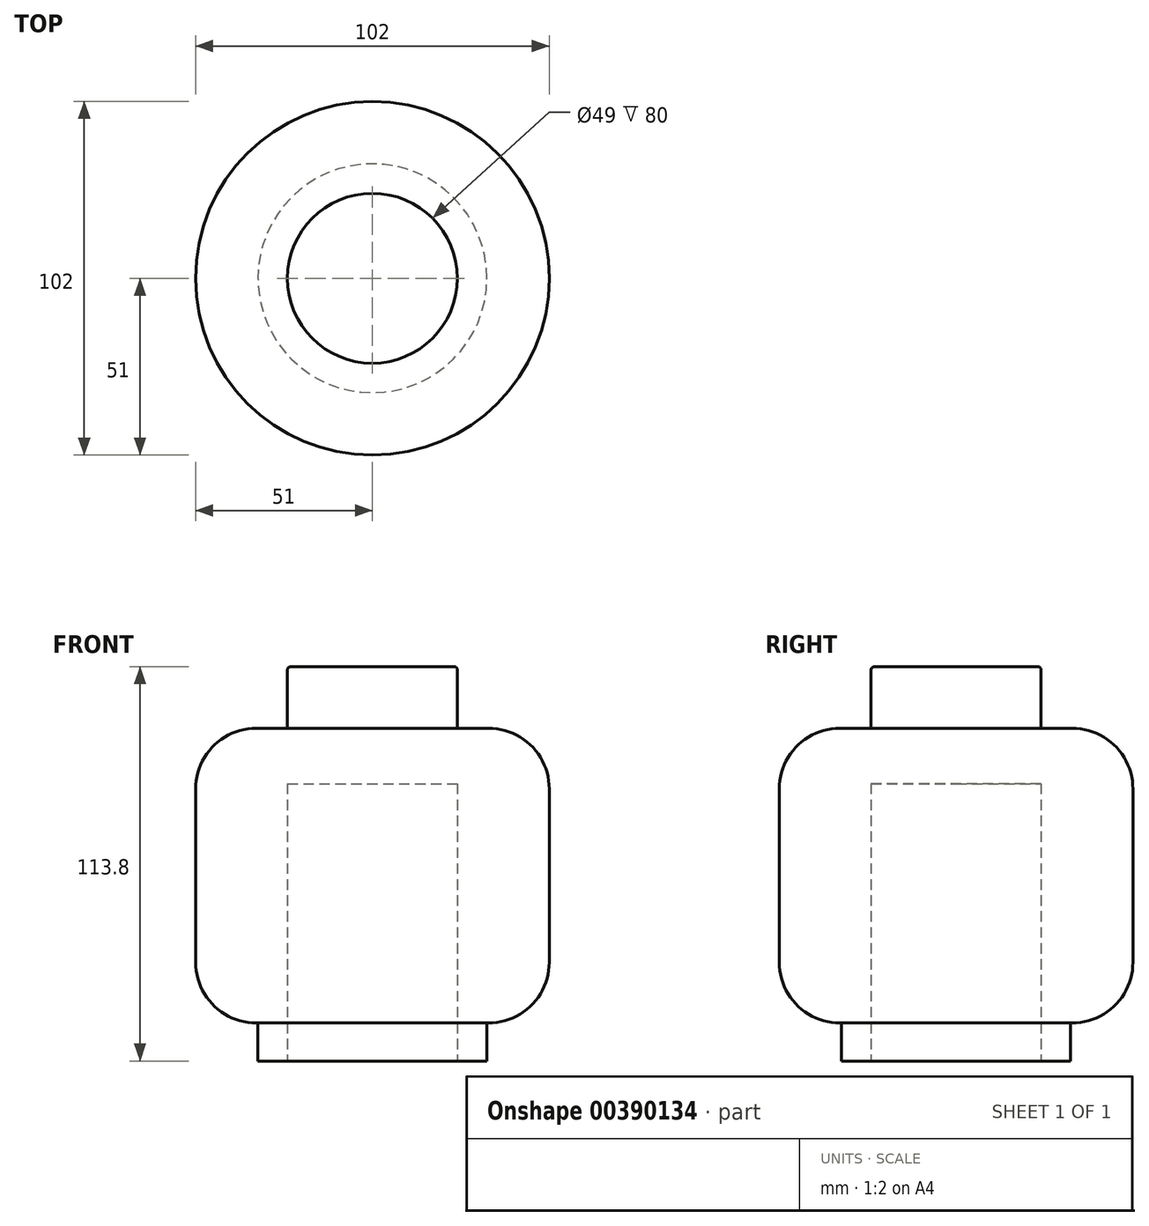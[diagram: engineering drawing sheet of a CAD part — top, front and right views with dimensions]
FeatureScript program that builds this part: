
annotation { "Feature Type Name" : "Feature", "Feature Type Description" : "" }
export const myFeature = defineFeature(function(context is Context, id is Id, definition is map)
    precondition{}
    {
        {
            var Q0;
            Q0=qCreatedBy(makeId("Top.planeOp"),FACE);
            var sketch = newSketch(context, id + "F0", { "sketchPlane" : qUnion([Q0])});
            skCircle(sketch, "E0", {"center": v(0, 0) * mm, "radius": 51 * mm});
            skSolve(sketch);
        }
        {
            var Q0;
            Q0=makeQuery(id+"F0.imprint","IMPRINT",FACE,{"disambiguationData":[TD([[makeQuery(id+"F0.imprint","IMPRINT",EDGE,{"derivedFrom":sQuery(id+"F0.wireOp",EDGE,"E0")}),1.0]])]});
            extrude(context, id + "F1", {"entities" : qUnion([Q0]), "flatOperationType" : FlatOperationType.REMOVE, "offsetDistance" : 25 * mm, "depth" : 42.5 * mm, "domain" : OperationDomain.MODEL});
        }
        {
            var Q0;
            Q0=makeQuery(id+"F1.opExtrude","CAP_FACE",FACE,{"disambiguationData":[OSD([sQuery(id+"F0.wireOp",EDGE,"E0")])],"isStart":false});
            fillet(context, id + "F2", {"entities" : qUnion([Q0]), "radius" : 17.5 * mm, "tangentPropagation" : true, "defaultsChanged" : false, "vertexSettings" : [], "allowEdgeOverflow" : false});
        }
        {
            var Q0;
            Q0=makeQuery(id+"F1.opExtrude","CAP_FACE",FACE,{"disambiguationData":[OSD([sQuery(id+"F0.wireOp",EDGE,"E0")])],"isStart":false});
            var sketch = newSketch(context, id + "F3", { "sketchPlane" : qUnion([Q0])});
            skCircle(sketch, "E1", {"center": v(0, 0) * mm, "radius": 24.5 * mm});
            skSolve(sketch);
        }
        {
            var Q0;
            Q0=makeQuery(id+"F3.imprint","IMPRINT",FACE,{"disambiguationData":[TD([[makeQuery(id+"F3.imprint","IMPRINT",EDGE,{"derivedFrom":sQuery(id+"F3.wireOp",EDGE,"E1")}),1.0]])]});
            extrude(context, id + "F4", {"entities" : qUnion([Q0]), "operationType" : NewBodyOperationType.ADD, "flatOperationType" : FlatOperationType.REMOVE, "offsetDistance" : 25 * mm, "depth" : 17.8 * mm, "domain" : OperationDomain.MODEL});
        }
        {
            var Q0;
            Q0=makeQuery(id+"F4.opExtrude","CAP_EDGE",EDGE,{"disambiguationData":[OSD([sQuery(id+"F3.wireOp",EDGE,"E1")])],"isStart":false});
            fillet(context, id + "F5", {"entities" : qUnion([Q0]), "radius" : 1 * mm, "tangentPropagation" : true, "defaultsChanged" : false, "vertexSettings" : [], "allowEdgeOverflow" : false});
        }
        {
            var Q0;
            Q0=makeQuery(id+"F1.opExtrude","CAP_FACE",FACE,{"disambiguationData":[OSD([sQuery(id+"F0.wireOp",EDGE,"E0")])],"isStart":true});
            extrude(context, id + "F6", {"entities" : qUnion([Q0]), "operationType" : NewBodyOperationType.ADD, "flatOperationType" : FlatOperationType.REMOVE, "offsetDistance" : 25 * mm, "depth" : 42.5 * mm, "domain" : OperationDomain.MODEL});
        }
        {
            var Q0;
            Q0=makeQuery(id+"F6.opExtrude","CAP_FACE",FACE,{"disambiguationData":[OSD([sQuery(id+"F0.wireOp",EDGE,"E0")])],"isStart":false});
            var sketch = newSketch(context, id + "F7", { "sketchPlane" : qUnion([Q0])});
            skCircle(sketch, "E2", {"center": v(0, 0) * mm, "radius": 33 * mm});
            skSolve(sketch);
        }
        {
            var Q0;
            Q0=makeQuery(id+"F7.imprint","IMPRINT",FACE,{"disambiguationData":[TD([[makeQuery(id+"F7.imprint","IMPRINT",EDGE,{"derivedFrom":sQuery(id+"F7.wireOp",EDGE,"E2")}),1.0]])]});
            extrude(context, id + "F8", {"entities" : qUnion([Q0]), "operationType" : NewBodyOperationType.ADD, "flatOperationType" : FlatOperationType.REMOVE, "depth" : 11 * mm, "offsetDistance" : 25 * mm, "domain" : OperationDomain.MODEL});
        }
        {
            var Q0;
            Q0=makeQuery(id+"F8.opExtrude","CAP_FACE",FACE,{"disambiguationData":[OSD([sQuery(id+"FBTceW7lFiRSeCQ_1.wireOp",EDGE,"hVqF75ZI-vp8t-1vhN-kkoJ-N5fIvlzN1McN"),sQuery(id+"F7.wireOp",EDGE,"E2")])],"isStart":false});
            var sketch = newSketch(context, id + "F9", { "sketchPlane" : qUnion([Q0])});
            skCircle(sketch, "E3", {"center": v(0, 0) * mm, "radius": 24.5 * mm});
            skSolve(sketch);
        }
        {
            var Q0;
            Q0=makeQuery(id+"F9.imprint","IMPRINT",FACE,{"disambiguationData":[TD([[makeQuery(id+"F9.imprint","IMPRINT",EDGE,{"derivedFrom":sQuery(id+"F9.wireOp",EDGE,"E3")}),1.0]])]});
            extrude(context, id + "F10", {"entities" : qUnion([Q0]), "operationType" : NewBodyOperationType.REMOVE, "oppositeDirection" : true, "depth" : 80 * mm, "offsetDistance" : 25 * mm});
        }
        {
            var Q0;
            Q0=makeQuery(id+"F6.opExtrude","CAP_EDGE",EDGE,{"disambiguationData":[OSD([sQuery(id+"F0.wireOp",EDGE,"E0")])],"isStart":false});
            fillet(context, id + "F11", {"entities" : qUnion([Q0]), "radius" : 17.5 * mm, "tangentPropagation" : true, "allowEdgeOverflow" : false});
        }
    });
